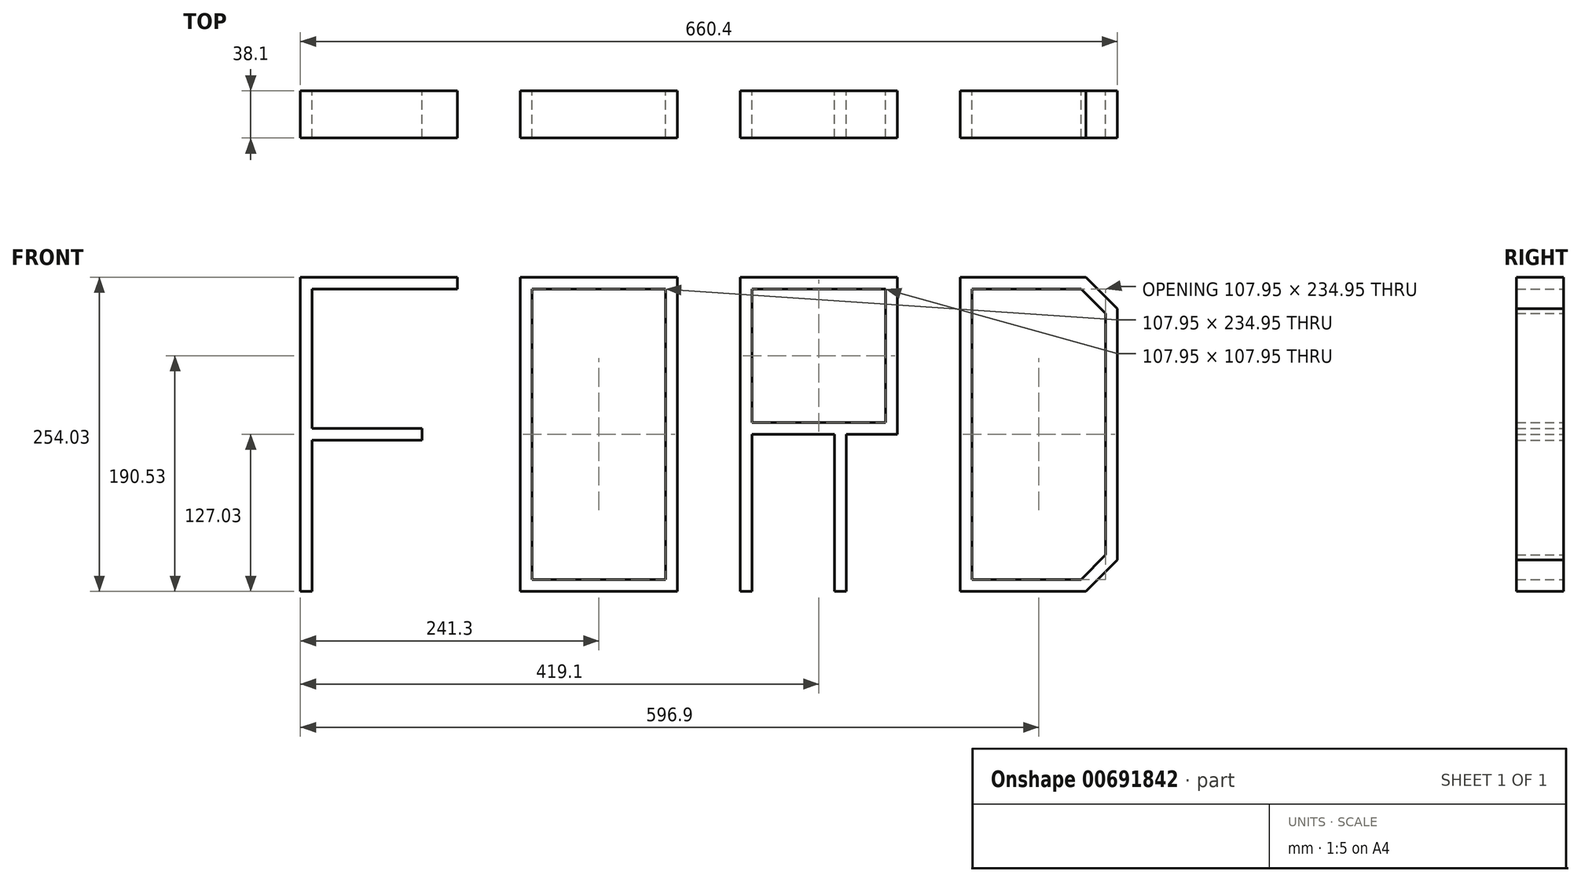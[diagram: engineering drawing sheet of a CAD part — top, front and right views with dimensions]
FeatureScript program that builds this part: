
annotation { "Feature Type Name" : "Feature", "Feature Type Description" : "" }
export const myFeature = defineFeature(function(context is Context, id is Id, definition is map)
    precondition{}
    {
        {
            var Q0;
            Q0=qCreatedBy(makeId("Front.planeOp"),FACE);
            var sketch = newSketch(context, id + "F0", { "sketchPlane" : qUnion([Q0])});
            skLineSegment(sketch, "E0", {"start": v(0, 0) * mm, "end": v(0, -254) * mm});
            skLineSegment(sketch, "E1", {"start": v(0, 0) * mm, "end": v(127, 0) * mm});
            skLineSegment(sketch, "E2", {"start": v(9.52, -131.78) * mm, "end": v(98.42, -131.78) * mm});
            skLineSegment(sketch, "E3", {"start": v(177.8, 0) * mm, "end": v(304.8, 0) * mm});
            skLineSegment(sketch, "E4", {"start": v(304.8, 0) * mm, "end": v(304.8, -254) * mm});
            skLineSegment(sketch, "E5", {"start": v(304.8, -254) * mm, "end": v(177.8, -254) * mm});
            skLineSegment(sketch, "E6", {"start": v(177.8, -254) * mm, "end": v(177.8, 0) * mm});
            skLineSegment(sketch, "E7", {"start": v(355.6, -254) * mm, "end": v(355.6, 0) * mm});
            skLineSegment(sketch, "E8", {"start": v(355.6, 0) * mm, "end": v(482.6, 0) * mm});
            skLineSegment(sketch, "E9", {"start": v(482.6, 0) * mm, "end": v(482.6, -127) * mm});
            skLineSegment(sketch, "E10", {"start": v(482.6, -127) * mm, "end": v(355.6, -127) * mm});
            skLineSegment(sketch, "E11", {"start": v(431.8, -127) * mm, "end": v(431.8, -254) * mm});
            skLineSegment(sketch, "E12", {"start": v(533.4, 0) * mm, "end": v(533.4, -254) * mm});
            skLineSegment(sketch, "E13", {"start": v(533.4, -254) * mm, "end": v(635, -254) * mm});
            skLineSegment(sketch, "E14", {"start": v(635, -254) * mm, "end": v(660.4, -228.6) * mm});
            skLineSegment(sketch, "E15", {"start": v(660.4, -228.6) * mm, "end": v(660.4, -25.4) * mm});
            skLineSegment(sketch, "E16", {"start": v(660.4, -25.4) * mm, "end": v(635, 0) * mm});
            skLineSegment(sketch, "E17", {"start": v(635, 0) * mm, "end": v(533.4, 0) * mm});
            skLineSegment(sketch, "E18.0", {"start": v(187.33, -9.52) * mm, "end": v(295.27, -9.52) * mm});
            skLineSegment(sketch, "E18.1", {"start": v(187.33, -244.48) * mm, "end": v(187.33, -9.52) * mm});
            skLineSegment(sketch, "E18.2", {"start": v(295.27, -244.47) * mm, "end": v(187.33, -244.48) * mm});
            skLineSegment(sketch, "E18.3", {"start": v(295.27, -9.52) * mm, "end": v(295.27, -244.47) * mm});
            skLineSegment(sketch, "E19.0", {"start": v(9.53, -9.53) * mm, "end": v(127, -9.53) * mm});
            skLineSegment(sketch, "E20", {"start": v(127, 0) * mm, "end": v(127, -9.53) * mm});
            skLineSegment(sketch, "E21", {"start": v(9.53, -122.25) * mm, "end": v(98.42, -122.25) * mm});
            skLineSegment(sketch, "E22", {"start": v(98.42, -122.25) * mm, "end": v(98.42, -131.78) * mm});
            skLineSegment(sketch, "E23", {"start": v(0, -254) * mm, "end": v(9.52, -254.03) * mm});
            skLineSegment(sketch, "E24", {"start": v(9.53, -9.52) * mm, "end": v(9.53, -122.25) * mm});
            skLineSegment(sketch, "E25", {"start": v(9.52, -254.03) * mm, "end": v(9.52, -131.78) * mm});
            skLineSegment(sketch, "E26.0", {"start": v(650.87, -29.35) * mm, "end": v(631.05, -9.52) * mm});
            skLineSegment(sketch, "E26.1", {"start": v(542.92, -9.52) * mm, "end": v(542.92, -244.47) * mm});
            skLineSegment(sketch, "E26.2", {"start": v(542.92, -244.47) * mm, "end": v(631.05, -244.47) * mm});
            skLineSegment(sketch, "E26.3", {"start": v(631.05, -9.52) * mm, "end": v(542.92, -9.52) * mm});
            skLineSegment(sketch, "E26.4", {"start": v(631.05, -244.47) * mm, "end": v(650.87, -224.65) * mm});
            skLineSegment(sketch, "E26.5", {"start": v(650.87, -224.65) * mm, "end": v(650.87, -29.35) * mm});
            skLineSegment(sketch, "E27", {"start": v(365.12, -9.52) * mm, "end": v(473.07, -9.52) * mm});
            skLineSegment(sketch, "E28", {"start": v(473.07, -9.52) * mm, "end": v(473.07, -117.47) * mm});
            skLineSegment(sketch, "E29", {"start": v(473.07, -117.47) * mm, "end": v(365.12, -117.47) * mm});
            skLineSegment(sketch, "E30", {"start": v(365.12, -117.47) * mm, "end": v(365.12, -9.52) * mm});
            skLineSegment(sketch, "E31", {"start": v(355.6, -254) * mm, "end": v(365.12, -254) * mm});
            skLineSegment(sketch, "E32", {"start": v(365.12, -254) * mm, "end": v(365.12, -127) * mm});
            skLineSegment(sketch, "E33", {"start": v(431.8, -254) * mm, "end": v(441.32, -254) * mm});
            skLineSegment(sketch, "E34", {"start": v(441.32, -254) * mm, "end": v(441.32, -127) * mm});
            skSolve(sketch);
        }
        {
            var Q0;
            Q0=makeQuery(id+"F0.imprint","IMPRINT",FACE,{"disambiguationData":[TD([[makeQuery(id+"F0.imprint","IMPRINT",EDGE,{"derivedFrom":sQuery(id+"F0.wireOp",EDGE,"E0")}),1.0]])]});
            var Q1;
            Q1=makeQuery(id+"F0.imprint","IMPRINT",FACE,{"disambiguationData":[TD([[makeQuery(id+"F0.imprint","IMPRINT",EDGE,{"derivedFrom":sQuery(id+"F0.wireOp",EDGE,"E3")}),-1.0]])]});
            var Q2;
            {var subQ0=sQuery(id+"F0.wireOp",EDGE,"E31");Q2=makeQuery(id+"F0.imprint","IMPRINT",FACE,{"disambiguationData":[TD([[makeQuery(id+"F0.imprint","IMPRINT",EDGE,{"derivedFrom":subQ0}),1.0]])]});}
            var Q3;
            {var subQ6=sQuery(id+"F0.wireOp",EDGE,"E8");Q3=makeQuery(id+"F0.imprint","IMPRINT",FACE,{"disambiguationData":[TD([[makeQuery(id+"F0.imprint","IMPRINT",EDGE,{"derivedFrom":subQ6}),-1.0]])]});}
            var Q4;
            {var subQ0=sQuery(id+"F0.wireOp",EDGE,"E11");Q4=makeQuery(id+"F0.imprint","IMPRINT",FACE,{"disambiguationData":[TD([[makeQuery(id+"F0.imprint","IMPRINT",EDGE,{"derivedFrom":subQ0}),1.0]])]});}
            var Q5;
            Q5=makeQuery(id+"F0.imprint","IMPRINT",FACE,{"disambiguationData":[TD([[makeQuery(id+"F0.imprint","IMPRINT",EDGE,{"derivedFrom":sQuery(id+"F0.wireOp",EDGE,"E12")}),1.0]])]});
            extrude(context, id + "F1", {"entities" : qUnion([Q0, Q1, Q2, Q3, Q4, Q5]), "depth" : 38.1 * mm, "offsetDistance" : 25.4 * mm});
        }
    });
